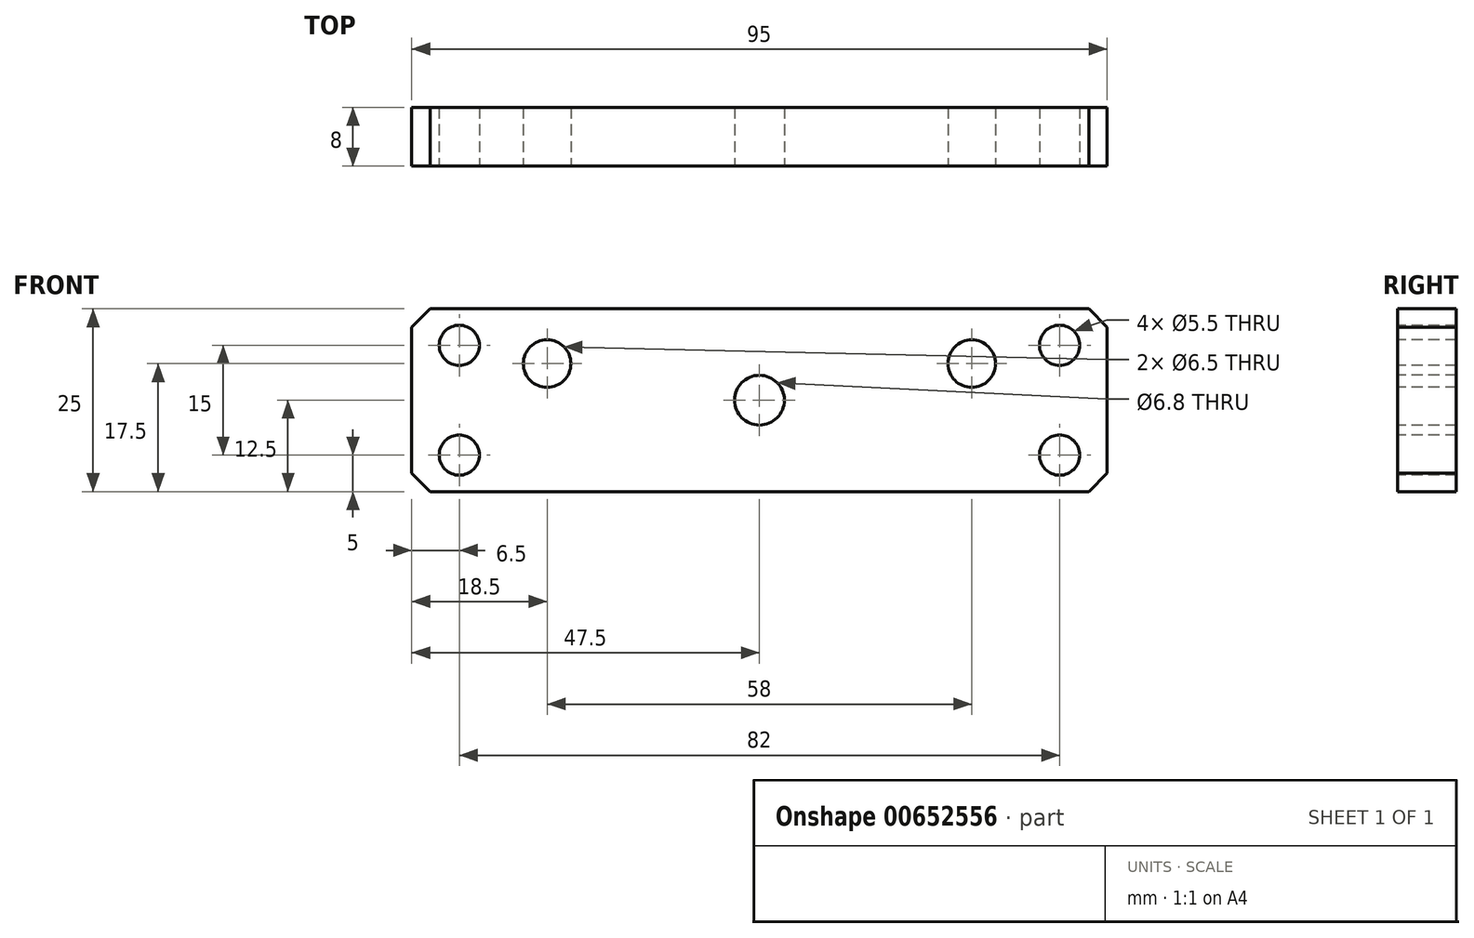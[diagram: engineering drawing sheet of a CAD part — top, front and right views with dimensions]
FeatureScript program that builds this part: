
annotation { "Feature Type Name" : "Feature", "Feature Type Description" : "" }
export const myFeature = defineFeature(function(context is Context, id is Id, definition is map)
    precondition{}
    {
        {
            var Q0;
            Q0=qCreatedBy(makeId("Front.planeOp"),FACE);
            var sketch = newSketch(context, id + "F0", { "sketchPlane" : qUnion([Q0])});
            skLineSegment(sketch, "E0.bottom", {"start": v(47.5, 12.5) * mm, "end": v(-47.5, 12.5) * mm});
            skLineSegment(sketch, "E0.top", {"start": v(47.5, -12.5) * mm, "end": v(-47.5, -12.5) * mm});
            skLineSegment(sketch, "E0.left", {"start": v(47.5, 12.5) * mm, "end": v(47.5, -12.5) * mm});
            skLineSegment(sketch, "E0.right", {"start": v(-47.5, 12.5) * mm, "end": v(-47.5, -12.5) * mm});
            skPoint(sketch, "E0.middle", {"position": v(0, 0) * mm});
            skSolve(sketch);
        }
        {
            var Q0;
            Q0 = qSketchRegion(id + "F0", true);
            extrude(context, id + "F1", {"entities" : qUnion([Q0]), "depth" : 8 * mm, "offsetDistance" : 25 * mm});
        }
        {
            var Q0;
            Q0=makeQuery(id+"F1.opExtrude","SWEPT_EDGE",EDGE,{"disambiguationData":[OSD([sQuery(id+"F0.wireOp",EDGE,"E0.bottom"),sQuery(id+"F0.wireOp",EDGE,"E0.left")])]});
            var Q1;
            Q1=makeQuery(id+"F1.opExtrude","SWEPT_EDGE",EDGE,{"disambiguationData":[OSD([sQuery(id+"F0.wireOp",EDGE,"E0.top"),sQuery(id+"F0.wireOp",EDGE,"E0.left")])]});
            var Q2;
            Q2=makeQuery(id+"F1.opExtrude","SWEPT_EDGE",EDGE,{"disambiguationData":[OSD([sQuery(id+"F0.wireOp",EDGE,"E0.bottom"),sQuery(id+"F0.wireOp",EDGE,"E0.right")])]});
            var Q3;
            Q3=makeQuery(id+"F1.opExtrude","SWEPT_EDGE",EDGE,{"disambiguationData":[OSD([sQuery(id+"F0.wireOp",EDGE,"E0.top"),sQuery(id+"F0.wireOp",EDGE,"E0.right")])]});
            chamfer(context, id + "F2", {"entities" : qUnion([Q0, Q1, Q2, Q3]), "width" : 2.5 * mm, "tangentPropagation" : true});
        }
        {
            var Q0;
            Q0=makeQuery(id+"F1.opExtrude","CAP_FACE",FACE,{"disambiguationData":[OSD([sQuery(id+"F0.wireOp",EDGE,"E0.bottom"),sQuery(id+"F0.wireOp",EDGE,"E0.top"),sQuery(id+"F0.wireOp",EDGE,"E0.left"),sQuery(id+"F0.wireOp",EDGE,"E0.right")])],"isStart":false});
            var sketch = newSketch(context, id + "F3", { "sketchPlane" : qUnion([Q0])});
            skPoint(sketch, "E1", {"position": v(-41, 7.5) * mm});
            skPoint(sketch, "E2", {"position": v(-41, -7.5) * mm});
            skPoint(sketch, "E3", {"position": v(41, 7.5) * mm});
            skPoint(sketch, "E4", {"position": v(41, -7.5) * mm});
            skSolve(sketch);
        }
        {
            var Q0;
            Q0=sQuery(id+"F3.wireOp",VERTEX,"E1");
            var Q1;
            Q1=sQuery(id+"F3.wireOp",VERTEX,"E2");
            var Q2;
            Q2=sQuery(id+"F3.wireOp",VERTEX,"E4");
            var Q3;
            Q3=sQuery(id+"F3.wireOp",VERTEX,"E3");
            var Q4;
            Q4=makeQuery(id+"F1.opExtrude","SWEPT_BODY",BODY,{"disambiguationData":[OSD([sQuery(id+"F0.wireOp",EDGE,"E0.bottom"),sQuery(id+"F0.wireOp",EDGE,"E0.top"),sQuery(id+"F0.wireOp",EDGE,"E0.left"),sQuery(id+"F0.wireOp",EDGE,"E0.right")])]});
            hole(context, id + "F4", {"style" : HoleStyle.SIMPLE, "endStyle" : HoleEndStyle.BLIND, "holeDiameter" : 5.5 * mm, "majorDiameter" : 5 * mm, "holeDepth" : 10 * mm, "isTappedThrough" : true, "tappedDepth" : 12 * mm, "tapClearance" : 3, "locations" : qUnion([Q0, Q1, Q2, Q3]), "scope" : qUnion([Q4])});
        }
        {
            var Q0;
            Q0=makeQuery(id+"F1.opExtrude","CAP_FACE",FACE,{"disambiguationData":[OSD([sQuery(id+"F0.wireOp",EDGE,"E0.bottom"),sQuery(id+"F0.wireOp",EDGE,"E0.top"),sQuery(id+"F0.wireOp",EDGE,"E0.left"),sQuery(id+"F0.wireOp",EDGE,"E0.right")])],"isStart":false});
            var sketch = newSketch(context, id + "F5", { "sketchPlane" : qUnion([Q0])});
            skPoint(sketch, "E5", {"position": v(-29, 5) * mm});
            skPoint(sketch, "E6", {"position": v(29, 5) * mm});
            skPoint(sketch, "E7", {"position": v(0, 0) * mm});
            skSolve(sketch);
        }
        {
            var Q0;
            Q0=sQuery(id+"F5.wireOp",VERTEX,"E5");
            var Q1;
            Q1=sQuery(id+"F5.wireOp",VERTEX,"E6");
            var Q2;
            Q2=makeQuery(id+"F1.opExtrude","SWEPT_BODY",BODY,{"disambiguationData":[OSD([sQuery(id+"F0.wireOp",EDGE,"E0.bottom"),sQuery(id+"F0.wireOp",EDGE,"E0.top"),sQuery(id+"F0.wireOp",EDGE,"E0.left"),sQuery(id+"F0.wireOp",EDGE,"E0.right")])]});
            hole(context, id + "F6", {"style" : HoleStyle.SIMPLE, "endStyle" : HoleEndStyle.BLIND, "holeDiameter" : 6.5 * mm, "majorDiameter" : 5 * mm, "holeDepth" : 10 * mm, "isTappedThrough" : true, "tappedDepth" : 12 * mm, "tapClearance" : 3, "locations" : qUnion([Q0, Q1]), "scope" : qUnion([Q2])});
        }
        {
            var Q0;
            Q0=sQuery(id+"F5.wireOp",VERTEX,"E7");
            var Q1;
            Q1=makeQuery(id+"F1.opExtrude","SWEPT_BODY",BODY,{"disambiguationData":[OSD([sQuery(id+"F0.wireOp",EDGE,"E0.bottom"),sQuery(id+"F0.wireOp",EDGE,"E0.top"),sQuery(id+"F0.wireOp",EDGE,"E0.left"),sQuery(id+"F0.wireOp",EDGE,"E0.right")])]});
            hole(context, id + "F7", {"style" : HoleStyle.SIMPLE, "endStyle" : HoleEndStyle.THROUGH, "standardTappedOrClearance" : lookupTablePath({ "standard" : "ISO", "engagement" : "75%", "pitch" : "1.25 mm", "size" : "M8", "type" : "Tapped" }), "standardBlindInLast" : lookupTablePath({ "standard" : "ISO", "engagement" : "75%", "pitch" : "1.25 mm", "size" : "M8", "type" : "Tapped" }), "holeDiameter" : 6.8 * mm, "majorDiameter" : 8 * mm, "showTappedDepth" : true, "isTappedThrough" : true, "tappedDepth" : 12 * mm, "tapClearance" : 3, "locations" : qUnion([Q0]), "scope" : qUnion([Q1])});
        }
    });
